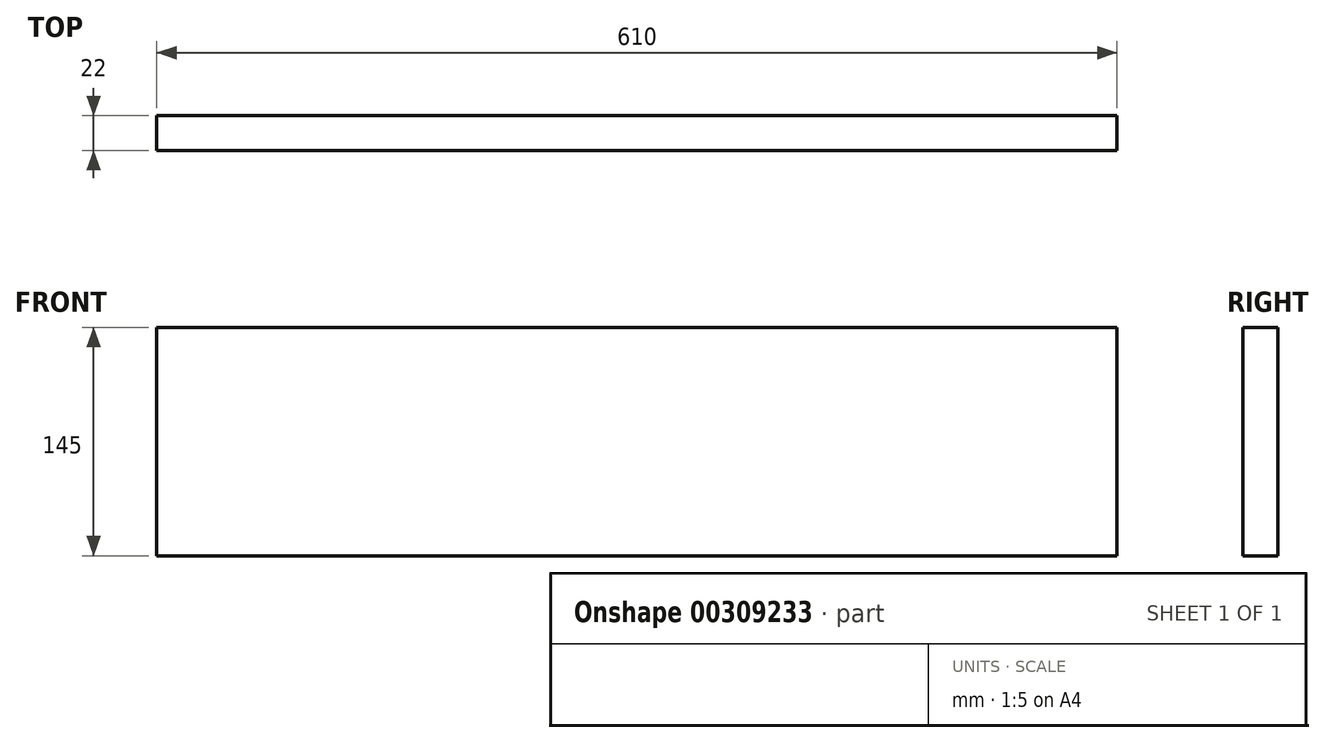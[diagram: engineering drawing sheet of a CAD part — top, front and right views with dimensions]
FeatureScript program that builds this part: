
annotation { "Feature Type Name" : "Feature", "Feature Type Description" : "" }
export const myFeature = defineFeature(function(context is Context, id is Id, definition is map)
    precondition{}
    {
        {
            var Q0;
            Q0=qCreatedBy(makeId("Right.planeOp"),FACE);
            var sketch = newSketch(context, id + "F0", { "sketchPlane" : qUnion([Q0])});
            skLineSegment(sketch, "E0.bottom", {"start": v(0, 0) * mm, "end": v(22, 0) * mm});
            skLineSegment(sketch, "E0.top", {"start": v(0, 145) * mm, "end": v(22, 145) * mm});
            skLineSegment(sketch, "E0.left", {"start": v(0, 0) * mm, "end": v(0, 145) * mm});
            skLineSegment(sketch, "E0.right", {"start": v(22, 0) * mm, "end": v(22, 145) * mm});
            skSolve(sketch);
        }
        {
            var Q0;
            Q0 = qSketchRegion(id + "F0", true);
            extrude(context, id + "F1", {"entities" : qUnion([Q0]), "oppositeDirection" : true, "depth" : 610 * mm});
        }
    });
